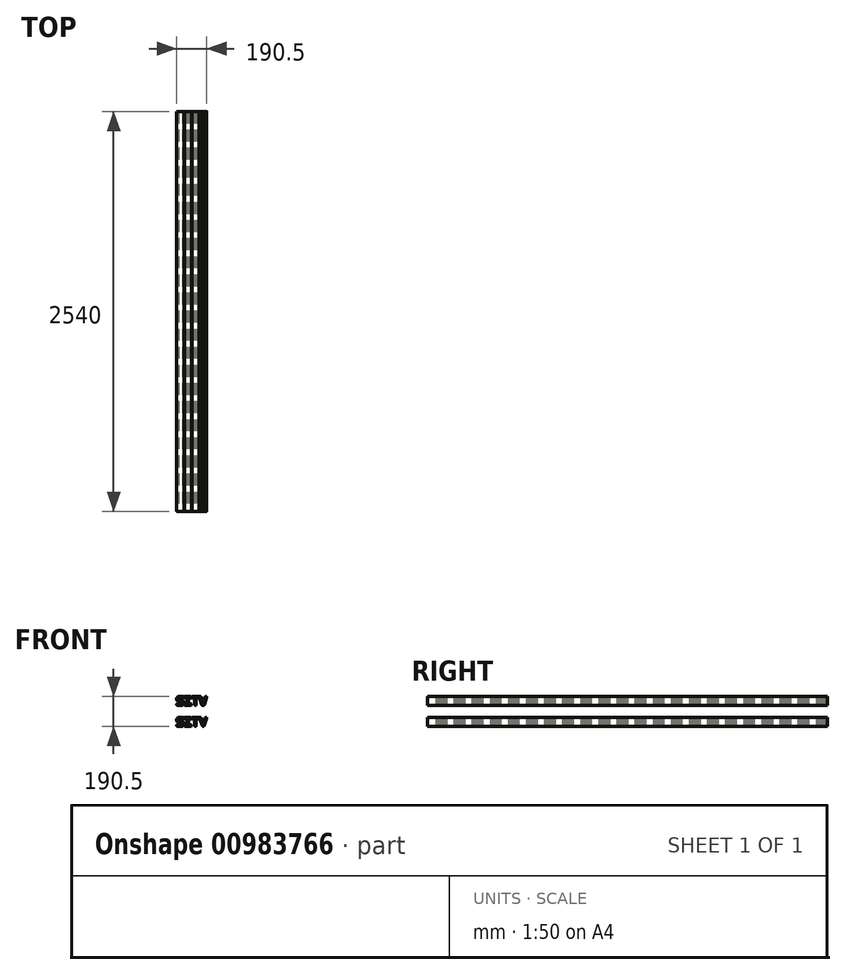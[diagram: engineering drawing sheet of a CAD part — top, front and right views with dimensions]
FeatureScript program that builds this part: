
annotation { "Feature Type Name" : "Feature", "Feature Type Description" : "" }
export const myFeature = defineFeature(function(context is Context, id is Id, definition is map)
    precondition{}
    {
        {
            var Q0;
            Q0=qCreatedBy(makeId("Front.planeOp"),FACE);
            var sketch = newSketch(context, id + "F0", { "sketchPlane" : qUnion([Q0])});
            skLineSegment(sketch, "E0", {"start": v(-40.64, 0) * mm, "end": v(-15.24, 0) * mm});
            skLineSegment(sketch, "E1", {"start": v(-40.64, 10.16) * mm, "end": v(-15.24, 10.16) * mm});
            skLineSegment(sketch, "E2", {"start": v(-40.64, 10.16) * mm, "end": v(-40.64, 0) * mm, "construction": true});
            skArc(sketch, "E3", {"start": v(-40.64, 10.16) * mm, "mid": v(-45.72, 5.08) * mm, "end": v(-40.64, 0) * mm});
            skLineSegment(sketch, "E4", {"start": v(0, 0) * mm, "end": v(-15.24, 0) * mm, "construction": true});
            skLineSegment(sketch, "E5", {"start": v(0, 15.24) * mm, "end": v(0, 18.41) * mm});
            skLineSegment(sketch, "E6", {"start": v(-10.16, 15.24) * mm, "end": v(-10.16, 18.41) * mm});
            skArc(sketch, "E7", {"start": v(0, 18.41) * mm, "mid": v(-4.46, 29.2) * mm, "end": v(-15.24, 33.66) * mm});
            skLineSegment(sketch, "E8", {"start": v(0, 18.41) * mm, "end": v(-15.24, 18.41) * mm, "construction": true});
            skLineSegment(sketch, "E9", {"start": v(-15.24, 18.41) * mm, "end": v(-15.24, 33.66) * mm, "construction": true});
            skArc(sketch, "E10", {"start": v(-10.16, 18.41) * mm, "mid": v(-11.65, 22) * mm, "end": v(-15.24, 23.5) * mm});
            skLineSegment(sketch, "E11", {"start": v(-15.24, 33.66) * mm, "end": v(-30.48, 33.66) * mm});
            skLineSegment(sketch, "E12", {"start": v(-15.24, 23.5) * mm, "end": v(-30.48, 23.5) * mm});
            skLineSegment(sketch, "E13", {"start": v(-30.48, 23.5) * mm, "end": v(-30.48, 38.73) * mm, "construction": true});
            skLineSegment(sketch, "E14", {"start": v(-30.48, 38.73) * mm, "end": v(-45.72, 38.73) * mm, "construction": true});
            skLineSegment(sketch, "E15", {"start": v(-15.24, 0) * mm, "end": v(-15.24, 15.24) * mm, "construction": true});
            skLineSegment(sketch, "E16", {"start": v(0, 15.24) * mm, "end": v(-15.24, 15.24) * mm, "construction": true});
            skLineSegment(sketch, "E17", {"start": v(0, 15.24) * mm, "end": v(0, 0) * mm, "construction": true});
            skArc(sketch, "E18", {"start": v(-15.24, 0) * mm, "mid": v(-4.46, 4.46) * mm, "end": v(0, 15.24) * mm});
            skArc(sketch, "E19", {"start": v(-15.24, 10.16) * mm, "mid": v(-11.65, 11.65) * mm, "end": v(-10.16, 15.24) * mm});
            skArc(sketch, "E20", {"start": v(-45.72, 38.73) * mm, "mid": v(-41.26, 27.96) * mm, "end": v(-30.48, 23.5) * mm});
            skArc(sketch, "E21", {"start": v(-35.56, 38.73) * mm, "mid": v(-34.07, 35.14) * mm, "end": v(-30.48, 33.66) * mm});
            skLineSegment(sketch, "E22", {"start": v(-40.64, 0) * mm, "end": v(-45.72, 0) * mm, "construction": true});
            skLineSegment(sketch, "E23", {"start": v(-45.72, 38.73) * mm, "end": v(-45.72, 41.9) * mm});
            skLineSegment(sketch, "E24", {"start": v(-35.56, 38.73) * mm, "end": v(-35.56, 41.9) * mm});
            skLineSegment(sketch, "E25", {"start": v(-45.72, 41.9) * mm, "end": v(-30.48, 41.9) * mm, "construction": true});
            skLineSegment(sketch, "E26", {"start": v(-30.48, 41.9) * mm, "end": v(-30.48, 57.15) * mm, "construction": true});
            skArc(sketch, "E27", {"start": v(-30.48, 57.15) * mm, "mid": v(-41.26, 52.69) * mm, "end": v(-45.72, 41.9) * mm});
            skArc(sketch, "E28", {"start": v(-30.48, 46.99) * mm, "mid": v(-34.07, 45.5) * mm, "end": v(-35.56, 41.9) * mm});
            skLineSegment(sketch, "E29", {"start": v(-30.48, 46.99) * mm, "end": v(-5.08, 46.99) * mm});
            skLineSegment(sketch, "E30", {"start": v(-30.48, 57.15) * mm, "end": v(-5.08, 57.15) * mm});
            skLineSegment(sketch, "E31", {"start": v(-5.08, 57.15) * mm, "end": v(-5.08, 46.99) * mm, "construction": true});
            skArc(sketch, "E32", {"start": v(-5.08, 46.99) * mm, "mid": v(0, 52.07) * mm, "end": v(-5.08, 57.15) * mm});
            skLineSegment(sketch, "E33", {"start": v(7.62, 0) * mm, "end": v(43.18, 0) * mm});
            skLineSegment(sketch, "E34", {"start": v(43.18, 0) * mm, "end": v(43.18, 10.16) * mm, "construction": true});
            skLineSegment(sketch, "E35", {"start": v(7.62, 0) * mm, "end": v(7.62, 10.16) * mm, "construction": true});
            skLineSegment(sketch, "E36", {"start": v(7.62, 10.16) * mm, "end": v(20.32, 10.16) * mm});
            skLineSegment(sketch, "E37", {"start": v(43.18, 10.16) * mm, "end": v(30.48, 10.16) * mm});
            skArc(sketch, "E38", {"start": v(7.62, 10.16) * mm, "mid": v(2.54, 5.08) * mm, "end": v(7.62, 0) * mm});
            skArc(sketch, "E39", {"start": v(43.18, 0) * mm, "mid": v(48.26, 5.08) * mm, "end": v(43.18, 10.16) * mm});
            skLineSegment(sketch, "E40", {"start": v(20.32, 10.16) * mm, "end": v(30.48, 10.16) * mm, "construction": true});
            skLineSegment(sketch, "E41", {"start": v(20.32, 10.16) * mm, "end": v(20.32, 47) * mm});
            skLineSegment(sketch, "E42", {"start": v(20.32, 47) * mm, "end": v(7.62, 47) * mm});
            skLineSegment(sketch, "E43", {"start": v(7.62, 47) * mm, "end": v(7.62, 57.15) * mm, "construction": true});
            skLineSegment(sketch, "E44", {"start": v(7.62, 57.15) * mm, "end": v(43.18, 57.15) * mm});
            skLineSegment(sketch, "E45", {"start": v(43.18, 57.15) * mm, "end": v(43.18, 47) * mm, "construction": true});
            skLineSegment(sketch, "E46", {"start": v(43.18, 47) * mm, "end": v(30.48, 47) * mm});
            skLineSegment(sketch, "E47", {"start": v(30.48, 47) * mm, "end": v(30.48, 10.16) * mm});
            skArc(sketch, "E48", {"start": v(7.62, 57.15) * mm, "mid": v(2.54, 52.07) * mm, "end": v(7.62, 46.99) * mm});
            skArc(sketch, "E49", {"start": v(43.18, 47) * mm, "mid": v(48.26, 52.07) * mm, "end": v(43.18, 57.15) * mm});
            skLineSegment(sketch, "E50", {"start": v(7.62, 47) * mm, "end": v(7.62, 10.16) * mm, "construction": true});
            skLineSegment(sketch, "E51", {"start": v(43.18, 47) * mm, "end": v(43.18, 10.16) * mm, "construction": true});
            skLineSegment(sketch, "E52", {"start": v(0, 0) * mm, "end": v(7.62, 0) * mm, "construction": true});
            skLineSegment(sketch, "E53", {"start": v(43.18, 57.15) * mm, "end": v(55.88, 57.15) * mm, "construction": true});
            skLineSegment(sketch, "E54", {"start": v(55.88, 57.15) * mm, "end": v(55.88, 46.99) * mm, "construction": true});
            skLineSegment(sketch, "E55", {"start": v(55.88, 47) * mm, "end": v(68.58, 47) * mm});
            skLineSegment(sketch, "E56", {"start": v(68.58, 47) * mm, "end": v(78.74, 47) * mm, "construction": true});
            skLineSegment(sketch, "E57", {"start": v(78.74, 47) * mm, "end": v(91.44, 47) * mm});
            skLineSegment(sketch, "E58", {"start": v(91.44, 46.99) * mm, "end": v(91.44, 57.15) * mm, "construction": true});
            skLineSegment(sketch, "E59", {"start": v(91.44, 57.15) * mm, "end": v(55.88, 57.15) * mm});
            skLineSegment(sketch, "E60", {"start": v(68.58, 46.99) * mm, "end": v(68.58, 5.08) * mm});
            skLineSegment(sketch, "E61", {"start": v(68.58, 5.08) * mm, "end": v(78.74, 5.08) * mm, "construction": true});
            skLineSegment(sketch, "E62", {"start": v(78.74, 5.08) * mm, "end": v(78.74, 46.99) * mm});
            skArc(sketch, "E63", {"start": v(55.88, 57.15) * mm, "mid": v(50.8, 52.07) * mm, "end": v(55.88, 46.99) * mm});
            skArc(sketch, "E64", {"start": v(91.44, 46.99) * mm, "mid": v(96.52, 52.07) * mm, "end": v(91.44, 57.15) * mm});
            skArc(sketch, "E65", {"start": v(68.58, 5.08) * mm, "mid": v(73.66, 0) * mm, "end": v(78.74, 5.08) * mm});
            skLineSegment(sketch, "E66", {"start": v(91.44, 57.15) * mm, "end": v(104.14, 57.15) * mm, "construction": true});
            skLineSegment(sketch, "E67", {"start": v(104.14, 57.15) * mm, "end": v(104.14, 52.07) * mm, "construction": true});
            skLineSegment(sketch, "E68", {"start": v(99.27, 50.62) * mm, "end": v(109, 53.52) * mm});
            skArc(sketch, "E69", {"start": v(109, 53.52) * mm, "mid": v(102.7, 56.94) * mm, "end": v(99.27, 50.62) * mm});
            skLineSegment(sketch, "E70", {"start": v(99.27, 50.62) * mm, "end": v(112.18, 7.26) * mm});
            skLineSegment(sketch, "E71", {"start": v(109, 53.52) * mm, "end": v(121.92, 10.16) * mm});
            skArc(sketch, "E72", {"start": v(112.18, 7.26) * mm, "mid": v(121.92, 0) * mm, "end": v(131.66, 7.26) * mm});
            skLineSegment(sketch, "E73", {"start": v(121.92, 10.16) * mm, "end": v(134.83, 53.52) * mm});
            skLineSegment(sketch, "E74", {"start": v(131.66, 7.26) * mm, "end": v(144.57, 50.62) * mm});
            skLineSegment(sketch, "E75", {"start": v(134.83, 53.52) * mm, "end": v(144.57, 50.62) * mm, "construction": true});
            skArc(sketch, "E76", {"start": v(144.57, 50.62) * mm, "mid": v(141.15, 56.94) * mm, "end": v(134.83, 53.52) * mm});
            skLineSegment(sketch, "E77", {"start": v(139.7, 52.07) * mm, "end": v(139.7, 57.15) * mm});
            skLineSegment(sketch, "E78", {"start": v(104.14, 57.15) * mm, "end": v(139.7, 57.15) * mm, "construction": true});
            skLineSegment(sketch, "E79", {"start": v(73.66, 0) * mm, "end": v(121.92, 0) * mm, "construction": true});
            skLineSegment(sketch, "E80", {"start": v(121.92, 10.16) * mm, "end": v(121.92, 0) * mm, "construction": true});
            skLineSegment(sketch, "E81", {"start": v(109, 53.52) * mm, "end": v(134.83, 53.52) * mm, "construction": true});
            skLineSegment(sketch, "E82", {"start": v(112.18, 7.26) * mm, "end": v(121.92, 10.16) * mm, "construction": true});
            skLineSegment(sketch, "E83", {"start": v(121.92, 10.16) * mm, "end": v(131.66, 7.26) * mm, "construction": true});
            skArc(sketch, "E84", {"start": v(121.69, 10.94) * mm, "mid": v(121.92, 10.88) * mm, "end": v(122.15, 10.94) * mm});
            skLineSegment(sketch, "E85", {"start": v(121.69, 10.94) * mm, "end": v(122.15, 10.94) * mm, "construction": true});
            skLineSegment(sketch, "E86", {"start": v(121.92, 11.43) * mm, "end": v(121.69, 10.94) * mm, "construction": true});
            skLineSegment(sketch, "E87", {"start": v(121.92, 11.43) * mm, "end": v(122.15, 10.94) * mm, "construction": true});
            skLineSegment(sketch, "E88", {"start": v(121.92, 10.16) * mm, "end": v(121.92, 11.43) * mm, "construction": true});
            skLineSegment(sketch, "E89", {"start": v(99.06, -76.2) * mm, "end": v(99.06, -133.35) * mm, "construction": true});
            skLineSegment(sketch, "E90", {"start": v(99.06, -133.35) * mm, "end": v(144.78, -133.35) * mm, "construction": true});
            skPoint(sketch, "E91", {"position": v(121.92, -133.35) * mm});
            skLineSegment(sketch, "E92", {"start": v(99.06, -76.2) * mm, "end": v(144.78, -76.2) * mm, "construction": true});
            skLineSegment(sketch, "E93", {"start": v(144.78, -76.2) * mm, "end": v(144.78, -133.35) * mm, "construction": true});
            skLineSegment(sketch, "E94", {"start": v(99.39, -83.08) * mm, "end": v(117.17, -130.07) * mm});
            skLineSegment(sketch, "E95", {"start": v(117.17, -130.07) * mm, "end": v(126.67, -126.47) * mm, "construction": true});
            skLineSegment(sketch, "E96", {"start": v(126.67, -126.47) * mm, "end": v(108.9, -79.48) * mm});
            skLineSegment(sketch, "E97", {"start": v(108.9, -79.48) * mm, "end": v(99.39, -83.08) * mm, "construction": true});
            skPoint(sketch, "E98", {"position": v(104.14, -81.28) * mm});
            skPoint(sketch, "E99", {"position": v(121.92, -128.27) * mm});
            skArc(sketch, "E100", {"start": v(108.9, -79.48) * mm, "mid": v(102.34, -76.53) * mm, "end": v(99.39, -83.08) * mm});
            skArc(sketch, "E101", {"start": v(117.17, -130.07) * mm, "mid": v(123.72, -133.02) * mm, "end": v(126.67, -126.47) * mm});
            skLineSegment(sketch, "E102", {"start": v(121.92, -128.27) * mm, "end": v(121.92, -133.35) * mm, "construction": true});
            skArc(sketch, "E103", {"start": v(144.45, -83.08) * mm, "mid": v(141.5, -76.53) * mm, "end": v(134.95, -79.48) * mm});
            skLineSegment(sketch, "E104", {"start": v(134.95, -79.48) * mm, "end": v(144.45, -83.08) * mm});
            skLineSegment(sketch, "E105", {"start": v(144.45, -83.08) * mm, "end": v(126.67, -130.07) * mm});
            skLineSegment(sketch, "E106", {"start": v(134.95, -79.48) * mm, "end": v(121.92, -113.92) * mm});
            skLineSegment(sketch, "E107", {"start": v(121.92, -128.27) * mm, "end": v(126.67, -130.07) * mm, "construction": true});
            skLineSegment(sketch, "E108", {"start": v(-40.64, -133.35) * mm, "end": v(-15.24, -133.35) * mm});
            skLineSegment(sketch, "E109", {"start": v(-40.64, -123.2) * mm, "end": v(-15.24, -123.2) * mm});
            skLineSegment(sketch, "E110", {"start": v(-40.64, -123.2) * mm, "end": v(-40.64, -133.35) * mm, "construction": true});
            skArc(sketch, "E111", {"start": v(-40.64, -123.2) * mm, "mid": v(-45.72, -128.27) * mm, "end": v(-40.64, -133.35) * mm});
            skLineSegment(sketch, "E112", {"start": v(0, -133.35) * mm, "end": v(-15.24, -133.35) * mm, "construction": true});
            skLineSegment(sketch, "E113", {"start": v(0, -118.11) * mm, "end": v(0, -114.94) * mm});
            skLineSegment(sketch, "E114", {"start": v(-10.16, -118.11) * mm, "end": v(-10.16, -114.94) * mm});
            skArc(sketch, "E115", {"start": v(0, -114.94) * mm, "mid": v(-4.46, -104.16) * mm, "end": v(-15.24, -99.7) * mm});
            skLineSegment(sketch, "E116", {"start": v(0, -114.94) * mm, "end": v(-15.24, -114.94) * mm, "construction": true});
            skLineSegment(sketch, "E117", {"start": v(-15.24, -114.93) * mm, "end": v(-15.24, -99.7) * mm, "construction": true});
            skArc(sketch, "E118", {"start": v(-10.16, -114.94) * mm, "mid": v(-11.65, -111.34) * mm, "end": v(-15.24, -109.85) * mm});
            skLineSegment(sketch, "E119", {"start": v(-15.24, -99.7) * mm, "end": v(-30.48, -99.7) * mm});
            skLineSegment(sketch, "E120", {"start": v(-15.24, -109.86) * mm, "end": v(-30.48, -109.86) * mm});
            skLineSegment(sketch, "E121", {"start": v(-30.48, -109.86) * mm, "end": v(-30.48, -94.62) * mm, "construction": true});
            skLineSegment(sketch, "E122", {"start": v(-30.48, -94.62) * mm, "end": v(-45.72, -94.62) * mm, "construction": true});
            skLineSegment(sketch, "E123", {"start": v(-15.24, -133.35) * mm, "end": v(-15.24, -118.11) * mm, "construction": true});
            skLineSegment(sketch, "E124", {"start": v(0, -118.11) * mm, "end": v(-15.24, -118.11) * mm, "construction": true});
            skLineSegment(sketch, "E125", {"start": v(0, -118.11) * mm, "end": v(0, -133.35) * mm, "construction": true});
            skArc(sketch, "E126", {"start": v(-15.24, -133.35) * mm, "mid": v(-4.46, -128.89) * mm, "end": v(0, -118.11) * mm});
            skArc(sketch, "E127", {"start": v(-15.24, -123.2) * mm, "mid": v(-11.65, -121.7) * mm, "end": v(-10.16, -118.11) * mm});
            skArc(sketch, "E128", {"start": v(-45.72, -94.62) * mm, "mid": v(-41.26, -105.4) * mm, "end": v(-30.48, -109.86) * mm});
            skArc(sketch, "E129", {"start": v(-35.56, -94.62) * mm, "mid": v(-34.07, -98.2) * mm, "end": v(-30.48, -99.7) * mm});
            skLineSegment(sketch, "E130", {"start": v(-40.64, -133.35) * mm, "end": v(-45.72, -133.35) * mm, "construction": true});
            skLineSegment(sketch, "E131", {"start": v(-45.72, -94.62) * mm, "end": v(-45.72, -91.44) * mm});
            skLineSegment(sketch, "E132", {"start": v(-35.56, -94.62) * mm, "end": v(-35.56, -91.44) * mm});
            skLineSegment(sketch, "E133", {"start": v(-45.72, -91.44) * mm, "end": v(-30.48, -91.44) * mm, "construction": true});
            skLineSegment(sketch, "E134", {"start": v(-30.48, -91.44) * mm, "end": v(-30.48, -76.2) * mm, "construction": true});
            skArc(sketch, "E135", {"start": v(-30.48, -76.2) * mm, "mid": v(-41.26, -80.66) * mm, "end": v(-45.72, -91.44) * mm});
            skArc(sketch, "E136", {"start": v(-30.48, -86.36) * mm, "mid": v(-34.07, -87.85) * mm, "end": v(-35.56, -91.44) * mm});
            skLineSegment(sketch, "E137", {"start": v(-30.48, -86.36) * mm, "end": v(-5.08, -86.36) * mm});
            skLineSegment(sketch, "E138", {"start": v(-30.48, -76.2) * mm, "end": v(-5.08, -76.2) * mm});
            skLineSegment(sketch, "E139", {"start": v(-5.08, -76.2) * mm, "end": v(-5.08, -86.36) * mm, "construction": true});
            skArc(sketch, "E140", {"start": v(-5.08, -86.36) * mm, "mid": v(0, -81.28) * mm, "end": v(-5.08, -76.2) * mm});
            skLineSegment(sketch, "E141", {"start": v(7.62, -133.35) * mm, "end": v(43.18, -133.35) * mm});
            skLineSegment(sketch, "E142", {"start": v(43.18, -133.35) * mm, "end": v(43.18, -123.2) * mm, "construction": true});
            skLineSegment(sketch, "E143", {"start": v(7.62, -133.35) * mm, "end": v(7.62, -123.2) * mm, "construction": true});
            skLineSegment(sketch, "E144", {"start": v(7.62, -123.2) * mm, "end": v(20.32, -123.2) * mm});
            skLineSegment(sketch, "E145", {"start": v(43.18, -123.2) * mm, "end": v(30.48, -123.2) * mm});
            skArc(sketch, "E146", {"start": v(7.62, -123.2) * mm, "mid": v(2.54, -128.27) * mm, "end": v(7.62, -133.35) * mm});
            skArc(sketch, "E147", {"start": v(43.18, -133.35) * mm, "mid": v(48.26, -128.27) * mm, "end": v(43.18, -123.2) * mm});
            skLineSegment(sketch, "E148", {"start": v(20.32, -123.2) * mm, "end": v(30.48, -123.2) * mm, "construction": true});
            skLineSegment(sketch, "E149", {"start": v(20.32, -123.2) * mm, "end": v(20.32, -86.36) * mm});
            skLineSegment(sketch, "E150", {"start": v(20.32, -86.36) * mm, "end": v(7.62, -86.36) * mm});
            skLineSegment(sketch, "E151", {"start": v(7.62, -86.36) * mm, "end": v(7.62, -76.2) * mm, "construction": true});
            skLineSegment(sketch, "E152", {"start": v(7.62, -76.2) * mm, "end": v(43.18, -76.2) * mm});
            skLineSegment(sketch, "E153", {"start": v(43.18, -76.2) * mm, "end": v(43.18, -86.36) * mm, "construction": true});
            skLineSegment(sketch, "E154", {"start": v(43.18, -86.36) * mm, "end": v(30.48, -86.36) * mm});
            skLineSegment(sketch, "E155", {"start": v(30.48, -86.36) * mm, "end": v(30.48, -123.2) * mm});
            skArc(sketch, "E156", {"start": v(7.62, -76.2) * mm, "mid": v(2.54, -81.28) * mm, "end": v(7.62, -86.36) * mm});
            skArc(sketch, "E157", {"start": v(43.18, -86.36) * mm, "mid": v(48.26, -81.28) * mm, "end": v(43.18, -76.2) * mm});
            skLineSegment(sketch, "E158", {"start": v(7.62, -86.36) * mm, "end": v(7.62, -123.2) * mm, "construction": true});
            skLineSegment(sketch, "E159", {"start": v(43.18, -86.36) * mm, "end": v(43.18, -123.2) * mm, "construction": true});
            skLineSegment(sketch, "E160", {"start": v(0, -133.35) * mm, "end": v(7.62, -133.35) * mm, "construction": true});
            skLineSegment(sketch, "E161", {"start": v(43.18, -76.2) * mm, "end": v(55.88, -76.2) * mm, "construction": true});
            skLineSegment(sketch, "E162", {"start": v(55.88, -76.2) * mm, "end": v(55.88, -86.36) * mm, "construction": true});
            skLineSegment(sketch, "E163", {"start": v(55.88, -86.36) * mm, "end": v(68.58, -86.36) * mm});
            skLineSegment(sketch, "E164", {"start": v(68.58, -86.36) * mm, "end": v(78.74, -86.36) * mm, "construction": true});
            skLineSegment(sketch, "E165", {"start": v(78.74, -86.36) * mm, "end": v(91.44, -86.36) * mm});
            skLineSegment(sketch, "E166", {"start": v(91.44, -86.36) * mm, "end": v(91.44, -76.2) * mm, "construction": true});
            skLineSegment(sketch, "E167", {"start": v(91.44, -76.2) * mm, "end": v(55.88, -76.2) * mm});
            skLineSegment(sketch, "E168", {"start": v(68.58, -86.36) * mm, "end": v(68.58, -128.27) * mm});
            skLineSegment(sketch, "E169", {"start": v(68.58, -128.27) * mm, "end": v(78.74, -128.27) * mm, "construction": true});
            skLineSegment(sketch, "E170", {"start": v(78.74, -128.27) * mm, "end": v(78.74, -86.36) * mm});
            skArc(sketch, "E171", {"start": v(55.88, -76.2) * mm, "mid": v(50.8, -81.28) * mm, "end": v(55.88, -86.36) * mm});
            skArc(sketch, "E172", {"start": v(91.44, -86.36) * mm, "mid": v(96.52, -81.28) * mm, "end": v(91.44, -76.2) * mm});
            skArc(sketch, "E173", {"start": v(68.58, -128.27) * mm, "mid": v(73.66, -133.35) * mm, "end": v(78.74, -128.27) * mm});
            skLineSegment(sketch, "E174", {"start": v(-45.72, 0) * mm, "end": v(-45.72, -76.2) * mm, "construction": true});
            skLineSegment(sketch, "E175", {"start": v(-30.48, -76.2) * mm, "end": v(-45.72, -76.2) * mm, "construction": true});
            skLineSegment(sketch, "E176", {"start": v(-45.72, -76.2) * mm, "end": v(-45.72, -91.44) * mm, "construction": true});
            skLineSegment(sketch, "E177", {"start": v(91.44, -76.2) * mm, "end": v(99.06, -76.2) * mm, "construction": true});
            skSolve(sketch);
        }
        {
            var Q0;
            Q0 = qSketchRegion(id + "F0", true);
            extrude(context, id + "F1", {"entities" : qUnion([Q0]), "oppositeDirection" : true, "depth" : 2540 * mm, "offsetDistance" : 25.4 * mm});
        }
    });
